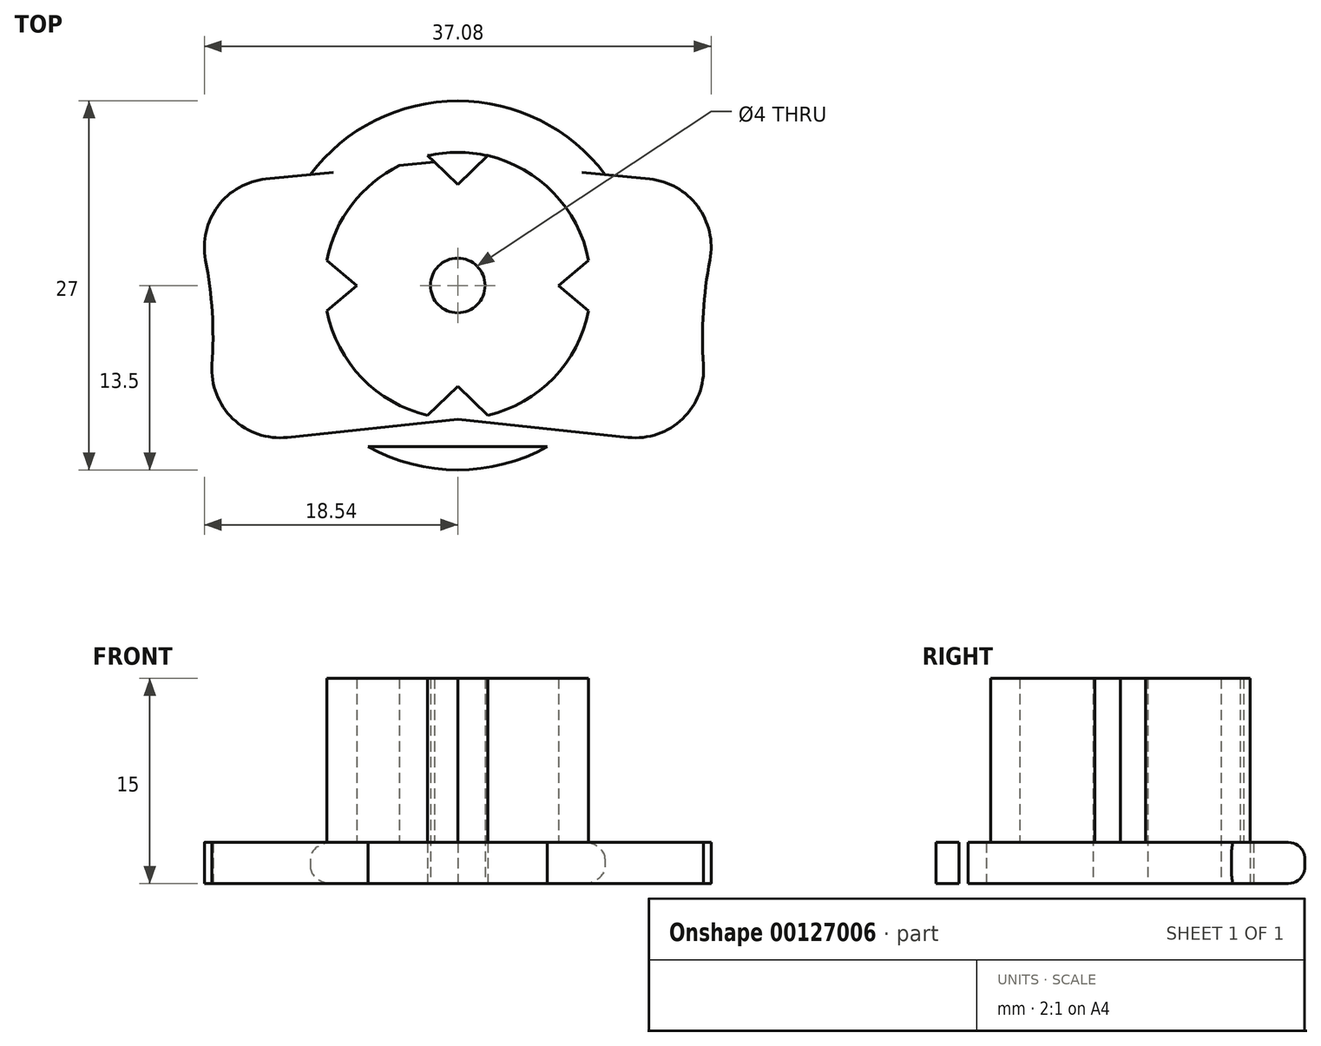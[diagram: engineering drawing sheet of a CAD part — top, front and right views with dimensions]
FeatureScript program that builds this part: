
annotation { "Feature Type Name" : "Feature", "Feature Type Description" : "" }
export const myFeature = defineFeature(function(context is Context, id is Id, definition is map)
    precondition{}
    {
        {
            var Q0;
            Q0=qCreatedBy(makeId("Top.planeOp"),FACE);
            var sketch = newSketch(context, id + "F0", { "sketchPlane" : qUnion([Q0])});
            skCircle(sketch, "E0", {"center": v(0, 0) * mm, "radius": 13.5 * mm});
            skCircle(sketch, "E1", {"center": v(0, 0) * mm, "radius": 9.75 * mm});
            skCircle(sketch, "E2", {"center": v(0, 0) * mm, "radius": 2 * mm});
            skLineSegment(sketch, "E3", {"start": v(19, -11.8) * mm, "end": v(0, -9.8) * mm});
            skLineSegment(sketch, "E4.MirrorCS", {"start": v(-19, -11.8) * mm, "end": v(0, -9.8) * mm});
            skArc(sketch, "E5", {"start": v(-19, -11.8) * mm, "mid": v(-17.95, -2.22) * mm, "end": v(-20, 7.2) * mm});
            skArc(sketch, "E6", {"start": v(20, 7.2) * mm, "mid": v(17.95, -2.22) * mm, "end": v(19, -11.8) * mm});
            skLineSegment(sketch, "E7", {"start": v(20, 7.2) * mm, "end": v(0, 9.2) * mm});
            skLineSegment(sketch, "E8", {"start": v(0, 9.2) * mm, "end": v(-20, 7.2) * mm});
            skLineSegment(sketch, "E9", {"start": v(0, 7.38) * mm, "end": v(-2.2, 9.5) * mm});
            skCircle(sketch, "E10", {"center": v(0, 0) * mm, "radius": 7.38 * mm});
            skLineSegment(sketch, "E11", {"start": v(-7.38, 0) * mm, "end": v(-9.57, 1.84) * mm});
            skLineSegment(sketch, "E12", {"start": v(-7.38, 0) * mm, "end": v(-9.57, -1.86) * mm});
            skLineSegment(sketch, "E13.MirrorCS", {"start": v(7.38, 0) * mm, "end": v(9.57, 1.84) * mm});
            skLineSegment(sketch, "E14.MirrorCS", {"start": v(7.38, 0) * mm, "end": v(9.57, -1.86) * mm});
            skLineSegment(sketch, "E15.MirrorCS", {"start": v(0, 7.38) * mm, "end": v(2.2, 9.5) * mm});
            skLineSegment(sketch, "E16.MirrorCS", {"start": v(0, -7.38) * mm, "end": v(2.2, -9.5) * mm});
            skLineSegment(sketch, "E17.MirrorCS", {"start": v(0, -7.38) * mm, "end": v(-2.2, -9.5) * mm});
            skLineSegment(sketch, "E18", {"start": v(19, -11.8) * mm, "end": v(-19, -11.8) * mm});
            skSolve(sketch);
        }
        {
            var Q0;
            {var subQ0=sQuery(id+"F0.wireOp",EDGE,"E14.MirrorCS");Q0=makeQuery(id+"F0.imprint","IMPRINT",FACE,{"disambiguationData":[TD([[makeQuery(id+"F0.imprint","IMPRINT",EDGE,{"derivedFrom":subQ0}),-1.0]])]});}
            var Q1;
            Q1=makeQuery(id+"F0.imprint","IMPRINT",FACE,{"disambiguationData":[TD([[makeQuery(id+"F0.imprint","IMPRINT",EDGE,{"derivedFrom":sQuery(id+"F0.wireOp",EDGE,"E2")}),-1.0]])]});
            var Q2;
            {var subQ0=sQuery(id+"F0.wireOp",EDGE,"E13.MirrorCS");Q2=makeQuery(id+"F0.imprint","IMPRINT",FACE,{"disambiguationData":[TD([[makeQuery(id+"F0.imprint","IMPRINT",EDGE,{"derivedFrom":subQ0}),1.0]])]});}
            var Q3;
            {var subQ0=sQuery(id+"F0.wireOp",EDGE,"E15.MirrorCS");Q3=makeQuery(id+"F0.imprint","IMPRINT",FACE,{"disambiguationData":[TD([[makeQuery(id+"F0.imprint","IMPRINT",EDGE,{"derivedFrom":subQ0}),-1.0]])]});}
            var Q4;
            {var subQ0=sQuery(id+"F0.wireOp",EDGE,"E9");Q4=makeQuery(id+"F0.imprint","IMPRINT",FACE,{"disambiguationData":[TD([[makeQuery(id+"F0.imprint","IMPRINT",EDGE,{"derivedFrom":subQ0}),1.0]])]});}
            var Q5;
            {var subQ0=sQuery(id+"F0.wireOp",EDGE,"E11");Q5=makeQuery(id+"F0.imprint","IMPRINT",FACE,{"disambiguationData":[TD([[makeQuery(id+"F0.imprint","IMPRINT",EDGE,{"derivedFrom":subQ0}),-1.0]])]});}
            var Q6;
            {var subQ0=sQuery(id+"F0.wireOp",EDGE,"E12");Q6=makeQuery(id+"F0.imprint","IMPRINT",FACE,{"disambiguationData":[TD([[makeQuery(id+"F0.imprint","IMPRINT",EDGE,{"derivedFrom":subQ0}),1.0]])]});}
            extrude(context, id + "F1", {"entities" : qUnion([Q0, Q1, Q2, Q3, Q4, Q5, Q6]), "depth" : 15 * mm});
        }
        {
            var Q0;
            {var subQ2=sQuery(id+"F0.wireOp",EDGE,"E8");var subQ4=sQuery(id+"F0.wireOp",EDGE,"E0");var subQ5=makeQuery(id+"F0.imprint","INTERSECT",VERTEX,{"derivedFrom":[subQ4,subQ2]});Q0=makeQuery(id+"F0.imprint","IMPRINT",FACE,{"disambiguationData":[TD([[makeQuery(id+"F0.imprint","IMPRINT",EDGE,{"disambiguationData":[TD([[subQ5,1.0]])],"derivedFrom":subQ4}),1.0]])]});}
            var Q1;
            {var subQ0=sQuery(id+"F0.wireOp",EDGE,"E9");Q1=makeQuery(id+"F0.imprint","IMPRINT",FACE,{"disambiguationData":[TD([[makeQuery(id+"F0.imprint","IMPRINT",EDGE,{"derivedFrom":subQ0}),-1.0]])]});}
            var Q2;
            {var subQ6=sQuery(id+"F0.wireOp",EDGE,"E0");var subQ11=sQuery(id+"F0.wireOp",EDGE,"E8");var subQ12=makeQuery(id+"F0.imprint","INTERSECT",VERTEX,{"derivedFrom":[subQ6,subQ11]});Q2=makeQuery(id+"F0.imprint","IMPRINT",FACE,{"disambiguationData":[TD([[makeQuery(id+"F0.imprint","IMPRINT",EDGE,{"disambiguationData":[TD([[subQ12,-1.0]])],"derivedFrom":subQ6}),1.0]])]});}
            var Q3;
            {var subQ5=sQuery(id+"F0.wireOp",EDGE,"E5");Q3=makeQuery(id+"F0.imprint","IMPRINT",FACE,{"disambiguationData":[TD([[makeQuery(id+"F0.imprint","IMPRINT",EDGE,{"derivedFrom":subQ5}),-1.0]])]});}
            var Q4;
            {var subQ0=sQuery(id+"F0.wireOp",EDGE,"E18");var subQ1=sQuery(id+"F0.wireOp",EDGE,"E0");var subQ2=makeQuery(id+"F0.imprint","INTERSECT",VERTEX,{"disambiguationData":[OD(0.0)],"derivedFrom":[subQ1,subQ0]});Q4=makeQuery(id+"F0.imprint","IMPRINT",FACE,{"disambiguationData":[TD([[makeQuery(id+"F0.imprint","IMPRINT",EDGE,{"disambiguationData":[TD([[subQ2,1.0]])],"derivedFrom":subQ1}),-1.0]])]});}
            var Q5;
            {var subQ0=sQuery(id+"F0.wireOp",EDGE,"E18");var subQ1=sQuery(id+"F0.wireOp",EDGE,"E0");var subQ2=makeQuery(id+"F0.imprint","INTERSECT",VERTEX,{"disambiguationData":[OD(1.0)],"derivedFrom":[subQ1,subQ0]});Q5=makeQuery(id+"F0.imprint","IMPRINT",FACE,{"disambiguationData":[TD([[makeQuery(id+"F0.imprint","IMPRINT",EDGE,{"disambiguationData":[TD([[subQ2,-1.0]])],"derivedFrom":subQ1}),-1.0]])]});}
            var Q6;
            {var subQ3=sQuery(id+"F0.wireOp",EDGE,"E0");var subQ5=sQuery(id+"F0.wireOp",EDGE,"E18");var subQ8=makeQuery(id+"F0.imprint","INTERSECT",VERTEX,{"disambiguationData":[OD(0.0)],"derivedFrom":[subQ3,subQ5]});Q6=makeQuery(id+"F0.imprint","IMPRINT",FACE,{"disambiguationData":[TD([[makeQuery(id+"F0.imprint","IMPRINT",EDGE,{"disambiguationData":[TD([[subQ8,1.0]])],"derivedFrom":subQ3}),1.0]])]});}
            var Q7;
            {var subQ5=sQuery(id+"F0.wireOp",EDGE,"E6");Q7=makeQuery(id+"F0.imprint","IMPRINT",FACE,{"disambiguationData":[TD([[makeQuery(id+"F0.imprint","IMPRINT",EDGE,{"derivedFrom":subQ5}),-1.0]])]});}
            var Q8;
            {var subQ0=sQuery(id+"F0.wireOp",EDGE,"E13.MirrorCS");Q8=makeQuery(id+"F0.imprint","IMPRINT",FACE,{"disambiguationData":[TD([[makeQuery(id+"F0.imprint","IMPRINT",EDGE,{"derivedFrom":subQ0}),-1.0]])]});}
            var Q9;
            {var subQ0=sQuery(id+"F0.wireOp",EDGE,"E11");Q9=makeQuery(id+"F0.imprint","IMPRINT",FACE,{"disambiguationData":[TD([[makeQuery(id+"F0.imprint","IMPRINT",EDGE,{"derivedFrom":subQ0}),1.0]])]});}
            var Q10;
            {var subQ0=sQuery(id+"F0.wireOp",EDGE,"E16.MirrorCS");Q10=makeQuery(id+"F0.imprint","IMPRINT",FACE,{"disambiguationData":[TD([[makeQuery(id+"F0.imprint","IMPRINT",EDGE,{"derivedFrom":subQ0}),-1.0]])]});}
            var Q11;
            {var subQ3=sQuery(id+"F0.wireOp",EDGE,"E9");var subQ5=sQuery(id+"F0.wireOp",EDGE,"E1");var subQ6=makeQuery(id+"F0.imprint","INTERSECT",VERTEX,{"derivedFrom":[subQ5,subQ3]});Q11=makeQuery(id+"F0.imprint","IMPRINT",FACE,{"disambiguationData":[TD([[makeQuery(id+"F0.imprint","IMPRINT",EDGE,{"disambiguationData":[TD([[subQ6,1.0]])],"derivedFrom":subQ5}),1.0]])]});}
            extrude(context, id + "F2", {"entities" : qUnion([Q0, Q1, Q2, Q3, Q4, Q5, Q6, Q7, Q8, Q9, Q10, Q11]), "operationType" : NewBodyOperationType.ADD, "depth" : 3 * mm});
        }
        {
            var Q0;
            Q0=makeQuery(id+"F2.opExtrude","SWEPT_EDGE",EDGE,{"disambiguationData":[OSD([sQuery(id+"F0.wireOp",EDGE,"E3"),sQuery(id+"F0.wireOp",EDGE,"E6"),sQuery(id+"F0.wireOp",EDGE,"E18")])]});
            fillet(context, id + "F3", {"entities" : qUnion([Q0]), "radius" : 5 * mm, "tangentPropagation" : true, "allowEdgeOverflow" : false});
        }
        {
            var Q0;
            Q0=makeQuery(id+"F2.opExtrude","SWEPT_EDGE",EDGE,{"disambiguationData":[OSD([sQuery(id+"F0.wireOp",EDGE,"E4.MirrorCS"),sQuery(id+"F0.wireOp",EDGE,"E5"),sQuery(id+"F0.wireOp",EDGE,"E18")])]});
            var Q1;
            Q1=makeQuery(id+"F2.opExtrude","SWEPT_EDGE",EDGE,{"disambiguationData":[OSD([sQuery(id+"F0.wireOp",EDGE,"E6"),sQuery(id+"F0.wireOp",EDGE,"E7")])]});
            var Q2;
            Q2=makeQuery(id+"F2.opExtrude","SWEPT_EDGE",EDGE,{"disambiguationData":[OSD([sQuery(id+"F0.wireOp",EDGE,"E5"),sQuery(id+"F0.wireOp",EDGE,"E8")])]});
            fillet(context, id + "F4", {"entities" : qUnion([Q0, Q1, Q2]), "radius" : 5 * mm, "tangentPropagation" : true, "allowEdgeOverflow" : false});
        }
        {
            var Q0;
            Q0=makeQuery(id+"F2.opExtrude","CAP_EDGE",EDGE,{"disambiguationData":[OSD([sQuery(id+"F0.wireOp",EDGE,"E18")])],"isStart":false});
            var Q1;
            Q1=makeQuery(id+"F2.opExtrude","CAP_EDGE",EDGE,{"disambiguationData":[OSD([sQuery(id+"F0.wireOp",EDGE,"E0")])],"isStart":false});
            var Q2;
            Q2=makeQuery(id+"F2.opExtrude","CAP_EDGE",EDGE,{"disambiguationData":[OSD([sQuery(id+"F0.wireOp",EDGE,"E18")])],"isStart":true});
            var Q3;
            Q3=makeQuery(id+"F2.opExtrude","CAP_EDGE",EDGE,{"disambiguationData":[OSD([sQuery(id+"F0.wireOp",EDGE,"E0")])],"isStart":true});
            fillet(context, id + "F5", {"entities" : qUnion([Q0, Q1, Q2, Q3]), "radius" : 1.2 * mm, "tangentPropagation" : true, "allowEdgeOverflow" : false});
        }
    });
